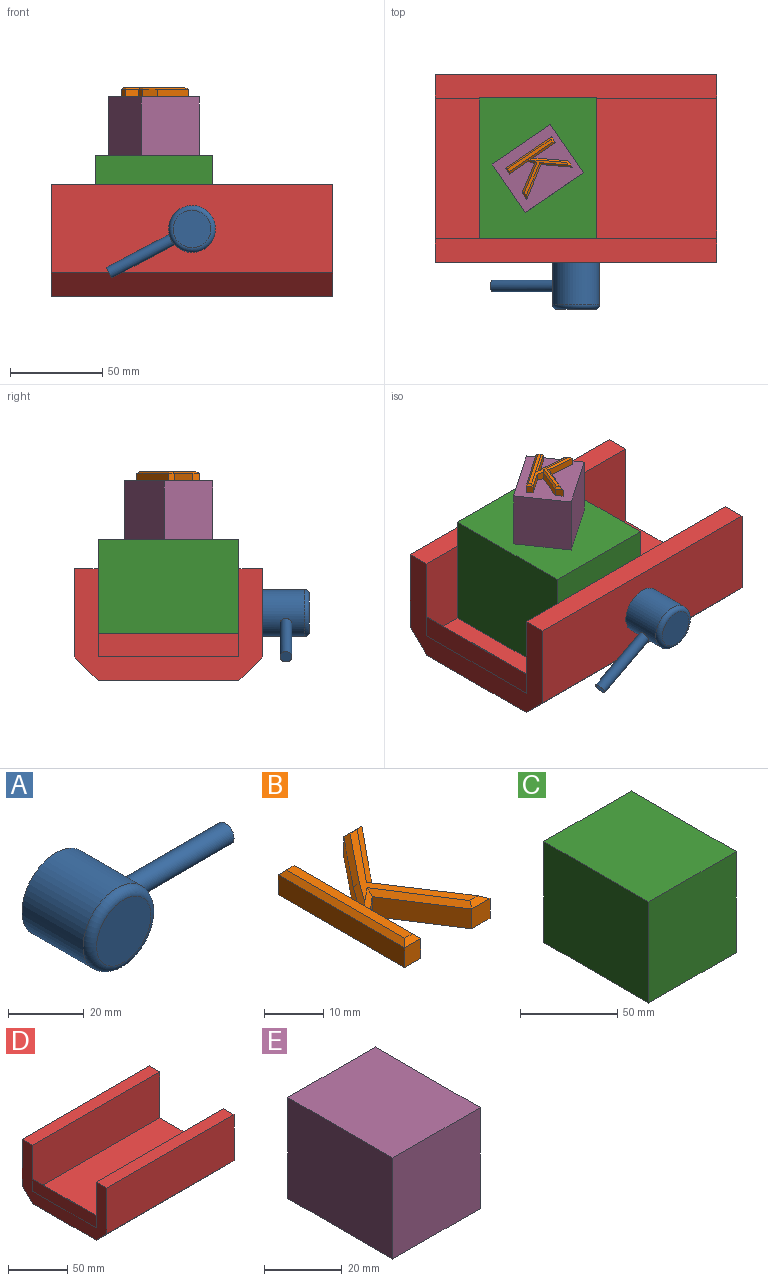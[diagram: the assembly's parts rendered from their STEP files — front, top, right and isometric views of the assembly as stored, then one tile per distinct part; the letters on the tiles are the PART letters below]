
ASSEMBLY  parts=5 mates=4
PART A: 6 faces, bbox 64.5x25.4x27.5 mm
  f0: cylinder r=12.7mm len=25.4mm, axis (0,1,0), area 1792.1mm2, adj f2,f3,f5
  f1: plane 20.32x20.32mm, normal (0,-1,0), area 324.3mm2, adj f5
  f2: plane 25.4x25.4mm, normal (0,1,0), area 506.7mm2, adj f0
  f3: cylinder r=3.17mm len=38.5mm, axis (-1,0,0), area 764.1mm2, adj f0,f4
  f4: plane 6.35x6.35mm, normal (1,0,0), area 31.7mm2, adj f3
  f5: torus R=10.16mm, axis (0,-1,0), area 295.2mm2, adj f0,f1
PART B: 28 faces, bbox 20.4x30.2x5.1 mm
  f0: plane 28.22x1.85mm, normal (0,0,1), area 52.2mm2, adj f16,f17,f18,f19
  f1: plane 4.37x4.08mm, normal (0,-1,0), area 17.8mm2, adj f2,f13,f15,f26
  f2: plane 17.05x11.15mm, normal (0.84,0.55,0), area 83.1mm2, adj f1,f3,f15,f27
  f3: plane 13.17x10.78mm, normal (0.77,-0.63,0), area 69.4mm2, adj f2,f4,f15,f25
  f4: plane 4.33x4.08mm, normal (0,1,0), area 17.6mm2, adj f3,f5,f15,f23
  f5: plane 11.64x9.36mm, normal (-0.78,0.63,0), area 60.9mm2, adj f4,f6,f15,f21
  f6: plane 4.08x3.47mm, normal (-0.81,0.58,0), area 17.5mm2, adj f5,f7,f15,f20
  f7: plane 15.11x4.08mm, normal (1,0,0), area 61.7mm2, adj f6,f8,f15,f19
  f8: plane 4.08x3.85mm, normal (0,1,0), area 15.7mm2, adj f7,f9,f15,f17
  f9: plane 30.22x4.08mm, normal (-1,0,0), area 123.3mm2, adj f8,f10,f15,f16
  f10: plane 4.08x3.85mm, normal (0,-1,0), area 15.7mm2, adj f9,f11,f15,f18
  f11: plane 12.07x4.08mm, normal (1,0,0), area 49.3mm2, adj f10,f12,f15,f19
  f12: plane 4.08x2.89mm, normal (0.63,-0.78,0), area 15.2mm2, adj f11,f13,f15,f22
  f13: plane 14.43x9.3mm, normal (-0.84,-0.54,0), area 70mm2, adj f1,f12,f15,f24
  f14: plane 28.22x14.77mm, normal (0,0,1), area 52.9mm2, adj f20,f21,f22,f23,f24,f25,f26,f27
  f15: plane 30.22x20.41mm, normal (0,0,-1), area 252.5mm2, adj f1,f2,f3,f4,f5,f6,f7,f8
  f16: plane 30.22x1mm, normal (-0.71,0,0.71), area 41.3mm2, adj f0,f9,f17,f18
  f17: plane 3.85x1mm, normal (0,0.71,0.71), area 4mm2, adj f0,f8,f16,f19
  f18: plane 3.85x1mm, normal (0,-0.71,0.71), area 4mm2, adj f0,f10,f16,f19
  f19: plane 30.22x1mm, normal (0.71,0,0.71), area 39.5mm2, adj f0,f7,f11,f17,f18,f20,f22
  f20: plane 6.11x4.15mm, normal (-0.57,0.41,0.71), area 8.1mm2, adj f6,f14,f19,f21,f22
  f21: plane 12.25x9.84mm, normal (-0.55,0.44,0.71), area 20.8mm2, adj f5,f14,f20,f23
  f22: plane 3.97x3.84mm, normal (0.45,-0.55,0.71), area 6.3mm2, adj f12,f14,f19,f20,f24
  f23: plane 4.33x1mm, normal (0,0.71,0.71), area 4.3mm2, adj f4,f14,f21,f25
  f24: plane 15.91x9.85mm, normal (-0.59,-0.38,0.71), area 24.7mm2, adj f13,f14,f22,f26
  f25: plane 13.17x12.01mm, normal (0.55,-0.45,0.71), area 23.1mm2, adj f3,f14,f23,f27
  f26: plane 4.37x1mm, normal (0,-0.71,0.71), area 4.5mm2, adj f1,f14,f24,f27
  f27: plane 17.12x12.38mm, normal (0.59,0.39,0.71), area 28mm2, adj f2,f14,f25,f26
PART C: 6 faces, bbox 63.5x76.2x63.5 mm
  f0: plane 76.2x63.5mm, normal (-1,0,0), area 4838.7mm2, adj f1,f3,f4,f5
  f1: plane 76.2x63.5mm, normal (0,0,-1), area 4838.7mm2, adj f0,f2,f4,f5
  f2: plane 76.2x63.5mm, normal (1,0,0), area 4838.7mm2, adj f1,f3,f4,f5
  f3: plane 76.2x63.5mm, normal (0,0,1), area 4838.7mm2, adj f0,f2,f4,f5
  f4: plane 63.5x63.5mm, normal (0,-1,0), area 4032.2mm2, adj f0,f1,f2,f3
  f5: plane 63.5x63.5mm, normal (0,1,0), area 4032.2mm2, adj f0,f1,f2,f3
PART D: 14 faces, bbox 152.4x101.6x60.3 mm
  f0: plane 152.4x47.63mm, normal (0,-1,0), area 7256.8mm2, adj f4,f7,f8,f11,f12,f13
  f1: plane 152.4x47.63mm, normal (0,-1,0), area 7258.1mm2, adj f2,f6,f7,f8
  f2: plane 152.4x12.7mm, normal (0,-0.71,-0.71), area 2737.2mm2, adj f1,f3,f7,f8
  f3: plane 152.4x76.2mm, normal (0,0,-1), area 11612.9mm2, adj f2,f7,f8,f10
  f4: plane 152.3x76.2mm, normal (0,0,1), area 11605.3mm2, adj f0,f5,f7,f13
  f5: plane 152.4x47.63mm, normal (0,1,0), area 7256.8mm2, adj f4,f6,f7,f8,f12,f13
  f6: plane 152.4x12.7mm, normal (0,0,1), area 1935.5mm2, adj f1,f5,f7,f8
  f7: plane 101.6x60.33mm, normal (1,0,0), area 2338.7mm2, adj f0,f1,f2,f3,f4,f5,f6,f9
  f8: plane 101.6x60.33mm, normal (-1,0,0), area 3306.4mm2, adj f0,f1,f2,f3,f5,f6,f9,f10
  f9: plane 152.4x47.63mm, normal (0,1,0), area 7258.1mm2, adj f7,f8,f10,f11
  f10: plane 152.4x12.7mm, normal (0,0.71,-0.71), area 2737.2mm2, adj f3,f7,f8,f9
  f11: plane 152.4x12.7mm, normal (0,0,1), area 1935.5mm2, adj f0,f7,f8,f9
  f12: plane 76.2x0.1mm, normal (0,0,1), area 7.6mm2, adj f0,f5,f8,f13
  f13: plane 76.2x12.7mm, normal (1,0,0), area 967.7mm2, adj f0,f4,f5,f12
PART E: 6 faces, bbox 31.8x38.1x31.8 mm
  f0: plane 31.75x31.75mm, normal (0,1,0), area 1008.1mm2, adj f1,f3,f4,f5
  f1: plane 38.1x31.75mm, normal (-1,0,0), area 1209.7mm2, adj f0,f2,f4,f5
  f2: plane 31.75x31.75mm, normal (0,-1,0), area 1008.1mm2, adj f1,f3,f4,f5
  f3: plane 38.1x31.75mm, normal (1,0,0), area 1209.7mm2, adj f0,f2,f4,f5
  f4: plane 38.1x31.75mm, normal (0,0,1), area 1209.7mm2, adj f0,f1,f2,f3
  f5: plane 38.1x31.75mm, normal (0,0,-1), area 1209.7mm2, adj f0,f1,f2,f3
PLACE A rot(axis=(0,1,0),152.2deg) t=(460.23,-50.8,-7.94)mm
PLACE B rot(axis=(0,0,-1),55.6deg) t=(442.21,0.28,63.5)mm
PLACE C t=(439.53,0,0)mm
PLACE D t=(460.23,0,0)mm fixed
PLACE E rot(axis=(0,0,-1),55.6deg) t=(439.53,0,47.62)mm
MATE revolute C.f3 <-> E.f5  axis (0,0,1) through (439.53,0,31.75)mm
MATE revolute A.f0 <-> D.f1  axis (0,1,0) through (460.23,-50.8,-7.94)mm
MATE slider C.f0 <-> D.f13  axis (-1,0,0) through (407.78,-38.1,-31.75)mm
MATE fastened E.f4 <-> B.f15  axis (0,0,1) through (439.53,0,63.5)mm
